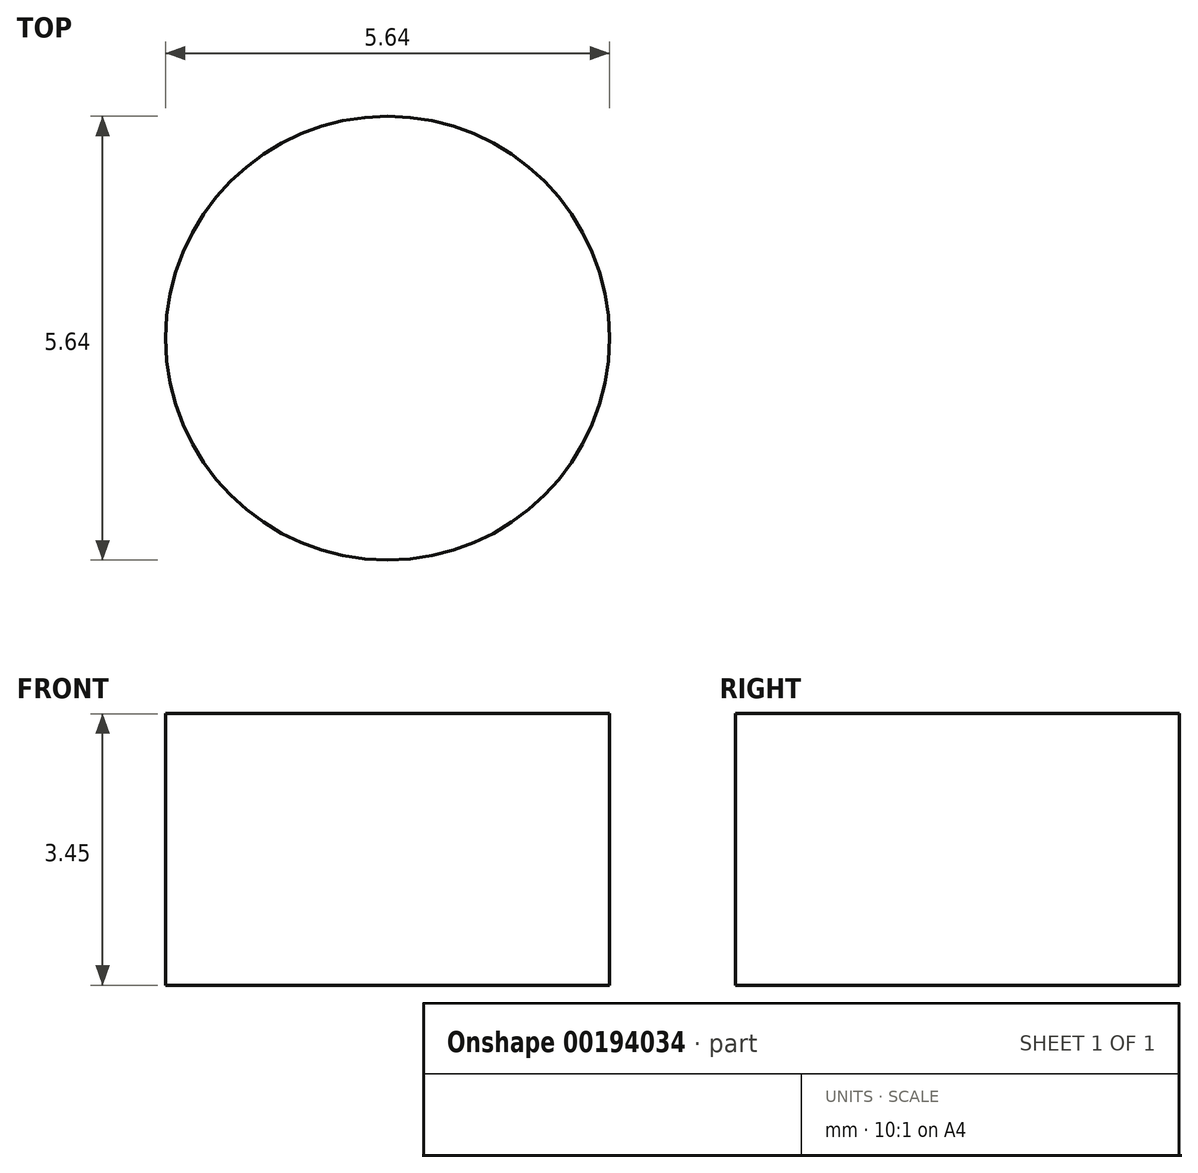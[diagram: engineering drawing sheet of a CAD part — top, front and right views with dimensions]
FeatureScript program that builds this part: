
annotation { "Feature Type Name" : "Feature", "Feature Type Description" : "" }
export const myFeature = defineFeature(function(context is Context, id is Id, definition is map)
    precondition{}
    {
        {
            var Q0;
            Q0=qCreatedBy(makeId("Top.planeOp"),FACE);
            var sketch = newSketch(context, id + "F0", { "sketchPlane" : qUnion([Q0])});
            skCircle(sketch, "E0", {"center": v(0, 0) * mm, "radius": 2.82 * mm});
            skSolve(sketch);
        }
        {
            var Q0;
            Q0 = qSketchRegion(id + "F0", true);
            extrude(context, id + "F1", {"entities" : qUnion([Q0]), "depth" : 3.45 * mm});
        }
    });
